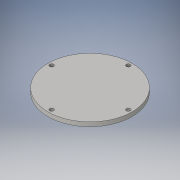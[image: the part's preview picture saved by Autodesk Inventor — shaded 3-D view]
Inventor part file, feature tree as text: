
AUTODESK INVENTOR PART (.ipt)
format: ipt  version: 2016 (Build 200138000, 138)  size: 100,352 bytes
history: native  units: in
note: dims shown in document units (in); Inventor stores cm internally (conversion verified against a paired STEP export)
features: sketch x2, extrude x1, hole x1
ambient origin geometry x8: Origin, YZ Plane, XZ Plane, XY Plane, X Axis, Y Axis, Z Axis, Center Point
bodies: Solid1 (feature_tree)
feature tree (4):
  extrude  "Extrusion1"  Depth=0.125in TaperAngle=0.0deg
  hole  "Hole1"  [1 undecoded]
  sketch  "Sketch1"  dims[d0=2.5in d1=0.125in d2=0.0in]
  sketch  "Sketch2"  dims[d3=1.14in d4=1.5748in d6=360.0deg d8=0.1181in d9=0.75in d10=0.375in d11=0.25in d12=0.5635in d13=1.0in d14=0.8108in]
note: 1 required parameter value undecoded (feature->parameter linkage not recoverable at this tier; creation-order binding heuristic only, values carry confidence <= 0.55)
